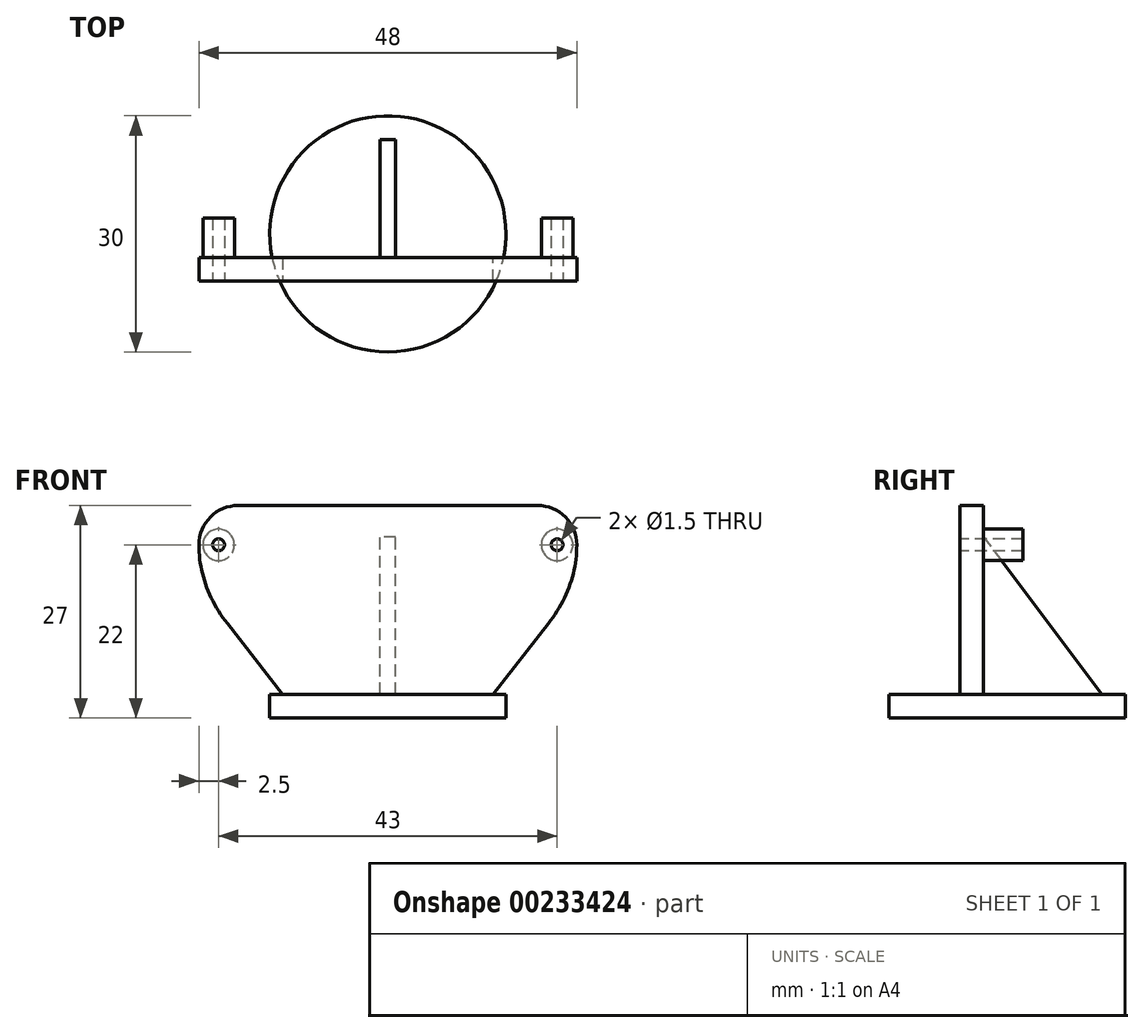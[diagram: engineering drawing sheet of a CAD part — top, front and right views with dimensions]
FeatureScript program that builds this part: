
annotation { "Feature Type Name" : "Feature", "Feature Type Description" : "" }
export const myFeature = defineFeature(function(context is Context, id is Id, definition is map)
    precondition{}
    {
        {
            var Q0;
            Q0=qCreatedBy(makeId("Top.planeOp"),FACE);
            var sketch = newSketch(context, id + "F0", { "sketchPlane" : qUnion([Q0])});
            skCircle(sketch, "E0", {"center": v(0, 0) * mm, "radius": 15 * mm});
            skSolve(sketch);
        }
        {
            var Q0;
            Q0 = qSketchRegion(id + "F0", true);
            extrude(context, id + "F1", {"entities" : qUnion([Q0]), "depth" : 3 * mm, "offsetDistance" : 25 * mm});
        }
        {
            var Q0;
            Q0=qCreatedBy(makeId("Front.planeOp"),FACE);
            cPlane(context, id + "F2", {"entities" : qUnion([Q0]), "cplaneType" : CPlaneType.OFFSET, "offset" : 6 * mm, "width" : 150 * mm, "height" : 150 * mm});
        }
        {
            var Q0;
            Q0=qCreatedBy(id+"F2.planeOp",FACE);
            var sketch = newSketch(context, id + "F3", { "sketchPlane" : qUnion([Q0])});
            skEllipticalArc(sketch, "E1", {});
            skLineSegment(sketch, "E2", {"start": v(-20.4, 11.98) * mm, "end": v(-11, 0) * mm});
            skLineSegment(sketch, "E3", {"start": v(-11, 0) * mm, "end": v(11, 0) * mm});
            skLineSegment(sketch, "E4", {"start": v(11, 0) * mm, "end": v(20.4, 11.98) * mm});
            skLineSegment(sketch, "E5", {"start": v(-21.5, 22) * mm, "end": v(21.5, 22) * mm, "construction": true});
            skCircle(sketch, "E6", {"center": v(-21.5, 22) * mm, "radius": 0.75 * mm});
            skCircle(sketch, "E7", {"center": v(21.5, 22) * mm, "radius": 0.75 * mm});
            skLineSegment(sketch, "E8", {"start": v(-19, 27) * mm, "end": v(19, 27) * mm});
            skPoint(sketch, "E9.visualSharp", {"position": v(-23.15, 27) * mm});
            skArc(sketch, "E9.filletArc", {"start": v(-19, 27) * mm, "mid": v(-22.54, 25.54) * mm, "end": v(-24, 22) * mm});
            skPoint(sketch, "E10.visualSharp", {"position": v(23.15, 27) * mm});
            skArc(sketch, "E10.filletArc", {"start": v(24, 22) * mm, "mid": v(22.54, 25.54) * mm, "end": v(19, 27) * mm});
            const initialGuessF3  = {"E1": [0, 0.022, 0, -1, 0.019, 0.024, 4.71238898038469, 1.5707963267948966]};
            skSetInitialGuess(sketch, initialGuessF3);
            skSolve(sketch);
        }
        {
            var Q0;
            Q0 = qSketchRegion(id + "F3", true);
            extrude(context, id + "F4", {"entities" : qUnion([Q0]), "operationType" : NewBodyOperationType.ADD, "oppositeDirection" : true, "depth" : 3 * mm, "offsetDistance" : 25 * mm});
        }
        {
            var Q0;
            Q0=qCreatedBy(makeId("Right.planeOp"),FACE);
            var sketch = newSketch(context, id + "F5", { "sketchPlane" : qUnion([Q0])});
            skLineSegment(sketch, "E11", {"start": v(12, 3) * mm, "end": v(-3, 3) * mm});
            skLineSegment(sketch, "E12", {"start": v(-3, 3) * mm, "end": v(-3, 23) * mm});
            skLineSegment(sketch, "E13", {"start": v(-3, 23) * mm, "end": v(12, 3) * mm});
            skSolve(sketch);
        }
        {
            var Q0;
            Q0=makeQuery(id+"F5.imprint","IMPRINT",FACE,{"disambiguationData":[TD([[makeQuery(id+"F5.imprint","IMPRINT",EDGE,{"derivedFrom":sQuery(id+"F5.wireOp",EDGE,"E11")}),-1.0]])]});
            extrude(context, id + "F6", {"entities" : qUnion([Q0]), "operationType" : NewBodyOperationType.ADD, "depth" : 2 * mm, "offsetDistance" : 25 * mm, "symmetric" : true});
        }
        {
            var Q0;
            Q0=makeQuery(id+"F4.opExtrude","CAP_FACE",FACE,{"disambiguationData":[OSD([sQuery(id+"F3.wireOp",EDGE,"E1"),sQuery(id+"F3.wireOp",EDGE,"E2"),sQuery(id+"F3.wireOp",EDGE,"E3"),sQuery(id+"F3.wireOp",EDGE,"E4"),sQuery(id+"F3.wireOp",EDGE,"E6"),sQuery(id+"F3.wireOp",EDGE,"E7"),sQuery(id+"F3.wireOp",EDGE,"E8"),sQuery(id+"F3.wireOp",EDGE,"E9.filletArc"),sQuery(id+"F3.wireOp",EDGE,"E10.filletArc")])],"isStart":false});
            var sketch = newSketch(context, id + "F7", { "sketchPlane" : qUnion([Q0])});
            skCircle(sketch, "E14", {"center": v(21.5, 22) * mm, "radius": 2 * mm});
            skCircle(sketch, "E15", {"center": v(-21.5, 22) * mm, "radius": 2 * mm});
            skSolve(sketch);
        }
        {
            var Q0;
            Q0=makeQuery(id+"F7.imprint","IMPRINT",FACE,{"disambiguationData":[TD([[makeQuery(id+"F7.imprint","IMPRINT",EDGE,{"derivedFrom":sQuery(id+"F7.wireOp",EDGE,"E15")}),1.0]])]});
            var Q1;
            Q1=makeQuery(id+"F7.imprint","IMPRINT",FACE,{"disambiguationData":[TD([[makeQuery(id+"F7.imprint","IMPRINT",EDGE,{"derivedFrom":sQuery(id+"F7.wireOp",EDGE,"E14")}),1.0]])]});
            extrude(context, id + "F8", {"entities" : qUnion([Q0, Q1]), "operationType" : NewBodyOperationType.ADD, "depth" : 5 * mm, "offsetDistance" : 25 * mm});
        }
    });
